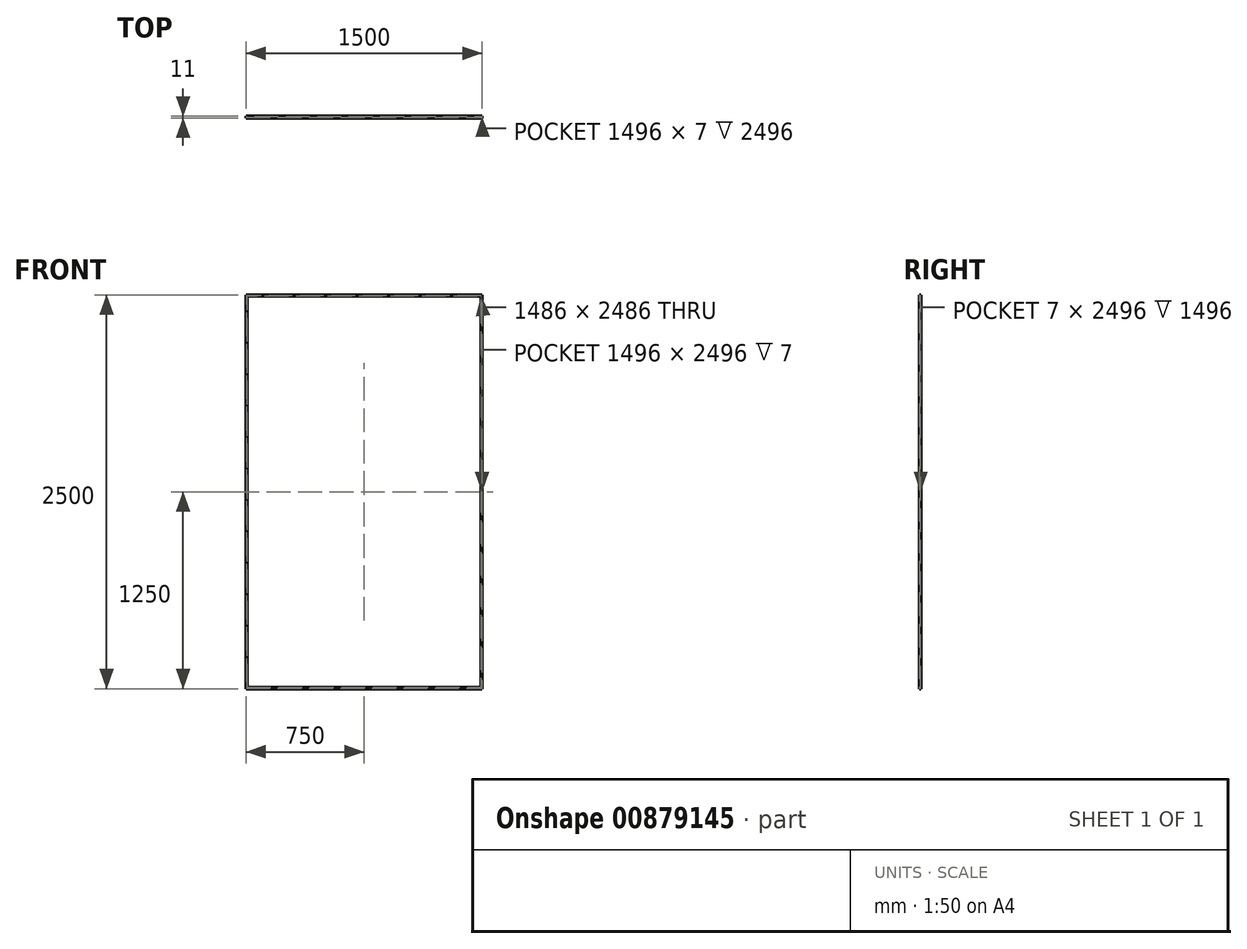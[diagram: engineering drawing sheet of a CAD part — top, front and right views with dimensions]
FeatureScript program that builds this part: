
annotation { "Feature Type Name" : "Feature", "Feature Type Description" : "" }
export const myFeature = defineFeature(function(context is Context, id is Id, definition is map)
    precondition{}
    {
        {
            var Q0;
            Q0=qCreatedBy(makeId("Front.planeOp"),FACE);
            var sketch = newSketch(context, id + "F0", { "sketchPlane" : qUnion([Q0])});
            skLineSegment(sketch, "E0.bottom", {"start": v(0, 0) * mm, "end": v(-1500, 0) * mm});
            skLineSegment(sketch, "E0.top", {"start": v(0, 2500) * mm, "end": v(-1500, 2500) * mm});
            skLineSegment(sketch, "E0.left", {"start": v(0, 0) * mm, "end": v(0, 2500) * mm});
            skLineSegment(sketch, "E0.right", {"start": v(-1500, 0) * mm, "end": v(-1500, 2500) * mm});
            skSolve(sketch);
        }
        {
            var Q0;
            Q0=makeQuery(id+"F0.imprint","IMPRINT",FACE,{"disambiguationData":[TD([[makeQuery(id+"F0.imprint","IMPRINT",EDGE,{"derivedFrom":sQuery(id+"F0.wireOp",EDGE,"E0.bottom")}),-1.0]])]});
            extrude(context, id + "F1", {"entities" : qUnion([Q0]), "endBound" : BoundingType.SYMMETRIC, "depth" : 2 * mm, "offsetDistance" : 25.4 * mm});
        }
        {
            var Q0;
            Q0=makeQuery(id+"F1.opExtrude","CAP_FACE",FACE,{"disambiguationData":[OSD([sQuery(id+"F0.wireOp",EDGE,"E0.bottom"),sQuery(id+"F0.wireOp",EDGE,"E0.top"),sQuery(id+"F0.wireOp",EDGE,"E0.left"),sQuery(id+"F0.wireOp",EDGE,"E0.right")])],"isStart":false});
            var sketch = newSketch(context, id + "F2", { "sketchPlane" : qUnion([Q0])});
            skLineSegment(sketch, "E1.bottom", {"start": v(-1500, 2500) * mm, "end": v(-1498, 2500) * mm});
            skLineSegment(sketch, "E1.top", {"start": v(-1500, 0) * mm, "end": v(-1498, 0) * mm});
            skLineSegment(sketch, "E1.left", {"start": v(-1500, 2500) * mm, "end": v(-1500, 0) * mm});
            skLineSegment(sketch, "E1.right", {"start": v(-1498, 2500) * mm, "end": v(-1498, 0) * mm});
            skLineSegment(sketch, "E2.bottom", {"start": v(0, 2500) * mm, "end": v(-2, 2500) * mm});
            skLineSegment(sketch, "E2.top", {"start": v(0, 0) * mm, "end": v(-2, 0) * mm});
            skLineSegment(sketch, "E2.left", {"start": v(0, 2500) * mm, "end": v(0, 0) * mm});
            skLineSegment(sketch, "E2.right", {"start": v(-2, 2500) * mm, "end": v(-2, 0) * mm});
            skLineSegment(sketch, "E3.bottom", {"start": v(-1500, 2500) * mm, "end": v(0, 2500) * mm});
            skLineSegment(sketch, "E3.top", {"start": v(-1500, 2498) * mm, "end": v(0, 2498) * mm});
            skLineSegment(sketch, "E3.left", {"start": v(-1500, 2500) * mm, "end": v(-1500, 2498) * mm});
            skLineSegment(sketch, "E3.right", {"start": v(0, 2500) * mm, "end": v(0, 2498) * mm});
            skLineSegment(sketch, "E4.bottom", {"start": v(-1500, 0) * mm, "end": v(0, 0) * mm});
            skLineSegment(sketch, "E4.top", {"start": v(-1500, 2) * mm, "end": v(0, 2) * mm});
            skLineSegment(sketch, "E4.left", {"start": v(-1500, 0) * mm, "end": v(-1500, 2) * mm});
            skLineSegment(sketch, "E4.right", {"start": v(0, 0) * mm, "end": v(0, 2) * mm});
            skSolve(sketch);
        }
        {
            var Q0;
            Q0 = qSketchRegion(id + "F2", true);
            extrude(context, id + "F3", {"entities" : qUnion([Q0]), "operationType" : NewBodyOperationType.ADD, "depth" : 7 * mm, "offsetDistance" : 25.4 * mm});
        }
        {
            var Q0;
            Q0=makeQuery(id+"F3.opExtrude","CAP_FACE",FACE,{"disambiguationData":[OSD([sQuery(id+"F2.wireOp",EDGE,"E1.left"),sQuery(id+"F2.wireOp",EDGE,"E1.right"),sQuery(id+"F2.wireOp",EDGE,"E2.left"),sQuery(id+"F2.wireOp",EDGE,"E2.right"),sQuery(id+"F2.wireOp",EDGE,"E3.bottom"),sQuery(id+"F2.wireOp",EDGE,"E3.top"),sQuery(id+"F2.wireOp",EDGE,"E3.left"),sQuery(id+"F2.wireOp",EDGE,"E3.right"),sQuery(id+"F2.wireOp",EDGE,"E4.bottom"),sQuery(id+"F2.wireOp",EDGE,"E4.top"),sQuery(id+"F2.wireOp",EDGE,"E4.left"),sQuery(id+"F2.wireOp",EDGE,"E4.right")])],"isStart":false});
            var sketch = newSketch(context, id + "F4", { "sketchPlane" : qUnion([Q0])});
            skLineSegment(sketch, "E5.bottom", {"start": v(-1500, 2500) * mm, "end": v(-1493, 2500) * mm});
            skLineSegment(sketch, "E5.top", {"start": v(-1500, 0) * mm, "end": v(-1493, 0) * mm});
            skLineSegment(sketch, "E5.left", {"start": v(-1500, 2500) * mm, "end": v(-1500, 0) * mm});
            skLineSegment(sketch, "E5.right", {"start": v(-1493, 2500) * mm, "end": v(-1493, 0) * mm});
            skLineSegment(sketch, "E6.bottom", {"start": v(-1500, 2500) * mm, "end": v(0, 2500) * mm});
            skLineSegment(sketch, "E6.top", {"start": v(-1500, 2493) * mm, "end": v(0, 2493) * mm});
            skLineSegment(sketch, "E6.left", {"start": v(-1500, 2500) * mm, "end": v(-1500, 2493) * mm});
            skLineSegment(sketch, "E6.right", {"start": v(0, 2500) * mm, "end": v(0, 2493) * mm});
            skLineSegment(sketch, "E7.bottom", {"start": v(0, 2500) * mm, "end": v(-7, 2500) * mm});
            skLineSegment(sketch, "E7.top", {"start": v(0, 0) * mm, "end": v(-7, 0) * mm});
            skLineSegment(sketch, "E7.left", {"start": v(0, 2500) * mm, "end": v(0, 0) * mm});
            skLineSegment(sketch, "E7.right", {"start": v(-7, 2500) * mm, "end": v(-7, 0) * mm});
            skLineSegment(sketch, "E8.bottom", {"start": v(-1500, 0) * mm, "end": v(0, 0) * mm});
            skLineSegment(sketch, "E8.top", {"start": v(-1500, 7) * mm, "end": v(0, 7) * mm});
            skLineSegment(sketch, "E8.left", {"start": v(-1500, 0) * mm, "end": v(-1500, 7) * mm});
            skLineSegment(sketch, "E8.right", {"start": v(0, 0) * mm, "end": v(0, 7) * mm});
            skSolve(sketch);
        }
        {
            var Q0;
            Q0 = qSketchRegion(id + "F4", true);
            extrude(context, id + "F5", {"entities" : qUnion([Q0]), "operationType" : NewBodyOperationType.ADD, "depth" : 2 * mm, "offsetDistance" : 25.4 * mm});
        }
    });
